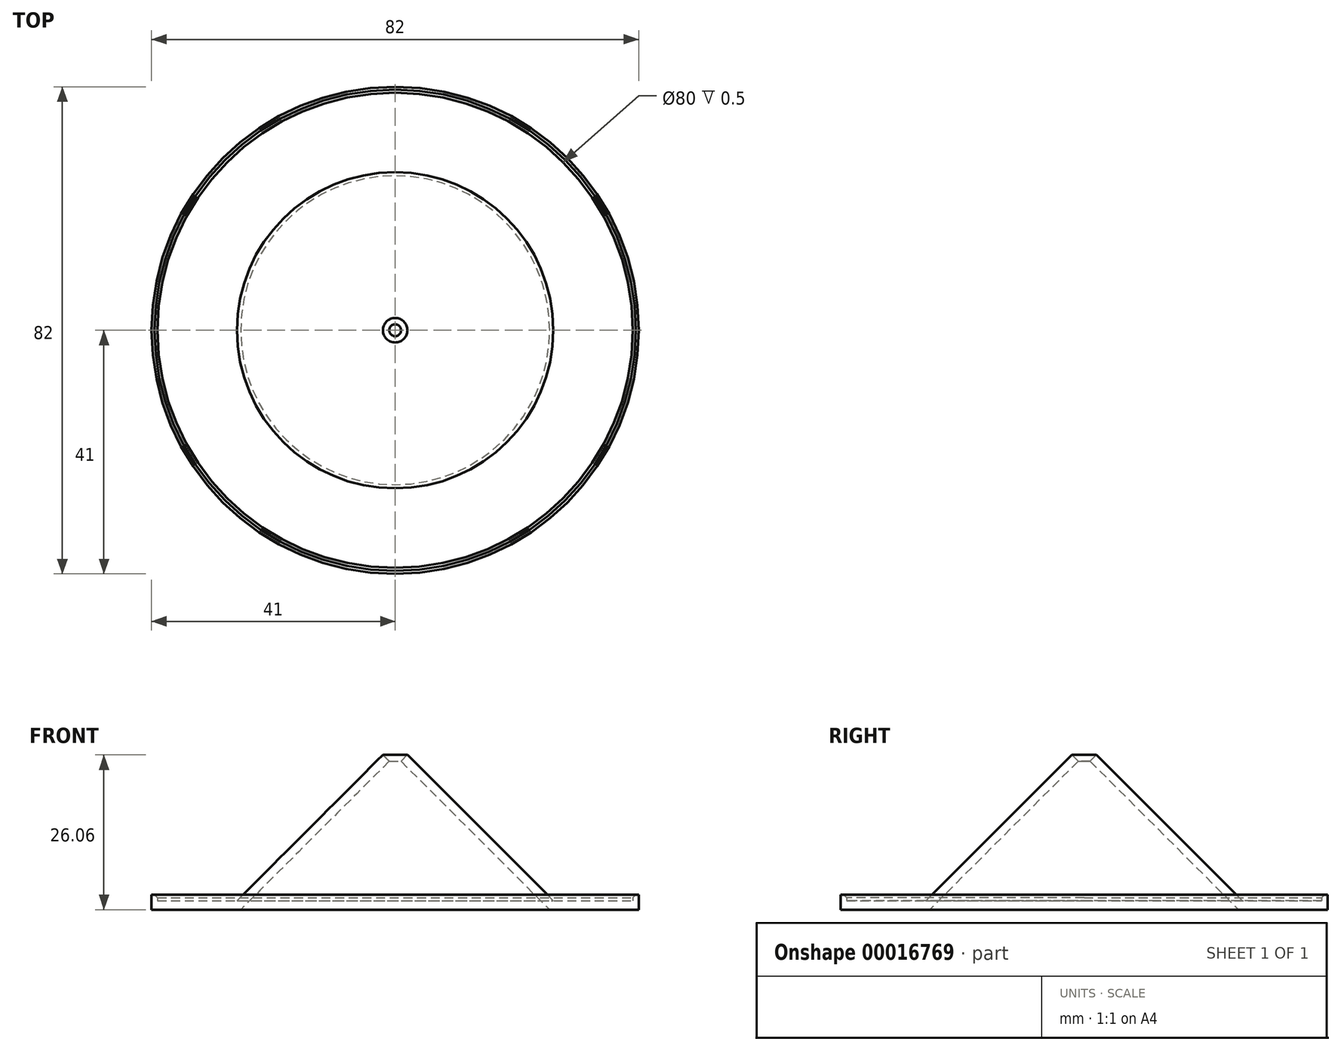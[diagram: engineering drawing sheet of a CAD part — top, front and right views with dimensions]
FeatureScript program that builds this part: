
annotation { "Feature Type Name" : "Feature", "Feature Type Description" : "" }
export const myFeature = defineFeature(function(context is Context, id is Id, definition is map)
    precondition{}
    {
        {
            var Q0;
            Q0=qCreatedBy(makeId("Front.planeOp"),FACE);
            var sketch = newSketch(context, id + "F0", { "sketchPlane" : qUnion([Q0])});
            skLineSegment(sketch, "E0", {"start": v(26, 0) * mm, "end": v(41, 0) * mm});
            skLineSegment(sketch, "E1", {"start": v(41, 0) * mm, "end": v(41, 1.5) * mm});
            skLineSegment(sketch, "E2", {"start": v(41, 1.5) * mm, "end": v(26.62, 1.5) * mm});
            skLineSegment(sketch, "E3", {"start": v(1, 0) * mm, "end": v(1, 25) * mm, "construction": true});
            skLineSegment(sketch, "E4", {"start": v(26, 0) * mm, "end": v(1, 25) * mm});
            skLineSegment(sketch, "E5", {"start": v(26.62, 1.5) * mm, "end": v(2.06, 26.06) * mm});
            skLineSegment(sketch, "E6", {"start": v(13.5, 12.5) * mm, "end": v(14.56, 13.56) * mm, "construction": true});
            skLineSegment(sketch, "E7", {"start": v(1, 25) * mm, "end": v(2.06, 26.06) * mm});
            skLineSegment(sketch, "E8", {"start": v(0, -10.57) * mm, "end": v(0, 32.48) * mm, "construction": true});
            skLineSegment(sketch, "E9", {"start": v(41, 1.5) * mm, "end": v(41, 2.5) * mm});
            skLineSegment(sketch, "E10", {"start": v(41, 2.5) * mm, "end": v(40, 2.5) * mm});
            skLineSegment(sketch, "E11", {"start": v(40, 2.5) * mm, "end": v(40, 1.5) * mm});
            skSolve(sketch);
        }
        {
            var Q0;
            Q0=makeQuery(id+"F0.imprint","IMPRINT",FACE,{"disambiguationData":[TD([[makeQuery(id+"F0.imprint","IMPRINT",EDGE,{"derivedFrom":sQuery(id+"F0.wireOp",EDGE,"E0")}),1.0]])]});
            var Q1;
            {var subQ1=sQuery(id+"F0.wireOp",EDGE,"E9");Q1=makeQuery(id+"F0.imprint","IMPRINT",FACE,{"disambiguationData":[TD([[makeQuery(id+"F0.imprint","IMPRINT",EDGE,{"derivedFrom":subQ1}),1.0]])]});}
            var Q2;
            Q2=sQuery(id+"F0.wireOp",EDGE,"E8");
            revolve(context, id + "F1", {"entities" : qUnion([Q0, Q1]), "axis" : qUnion([Q2]), "revolveType" : RevolveType.FULL});
        }
        {
            var Q0;
            Q0=makeQuery(id+"F1.opRevolve","SWEPT_EDGE",EDGE,{"disambiguationData":[OSD([sQuery(id+"F0.wireOp",EDGE,"E10"),sQuery(id+"F0.wireOp",EDGE,"E11")])]});
            chamfer(context, id + "F2", {"entities" : qUnion([Q0]), "width" : .5 * mm, "tangentPropagation" : true});
        }
    });
